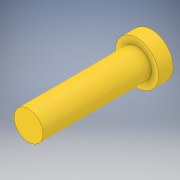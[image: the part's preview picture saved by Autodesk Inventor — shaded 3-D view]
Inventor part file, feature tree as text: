
AUTODESK INVENTOR PART (.ipt)
format: ipt  version: 2018 (Build 220112000, 112)  size: 103,424 bytes
history: native  units: in
note: dims shown in document units (in); Inventor stores cm internally (conversion verified against a paired STEP export)
features: sketch x3, extrude x2
ambient origin geometry x8: Origin, YZ Plane, XZ Plane, XY Plane, X Axis, Y Axis, Z Axis, Center Point
bodies: Solid1 (feature_tree)
feature tree (5):
  extrude  "Extrusion1"  Depth=0.3937in TaperAngle=0.0deg
  extrude  "Extrusion2"  Depth=2.9528in TaperAngle=0.0deg
  sketch  "Sketch3"
  sketch  "Sketch1"  dims[d0=1.1811in d1=0.3937in d2=0.0in]
  sketch  "Sketch2"  dims[d3=0.7874in d4=2.9528in d5=0.0in]
